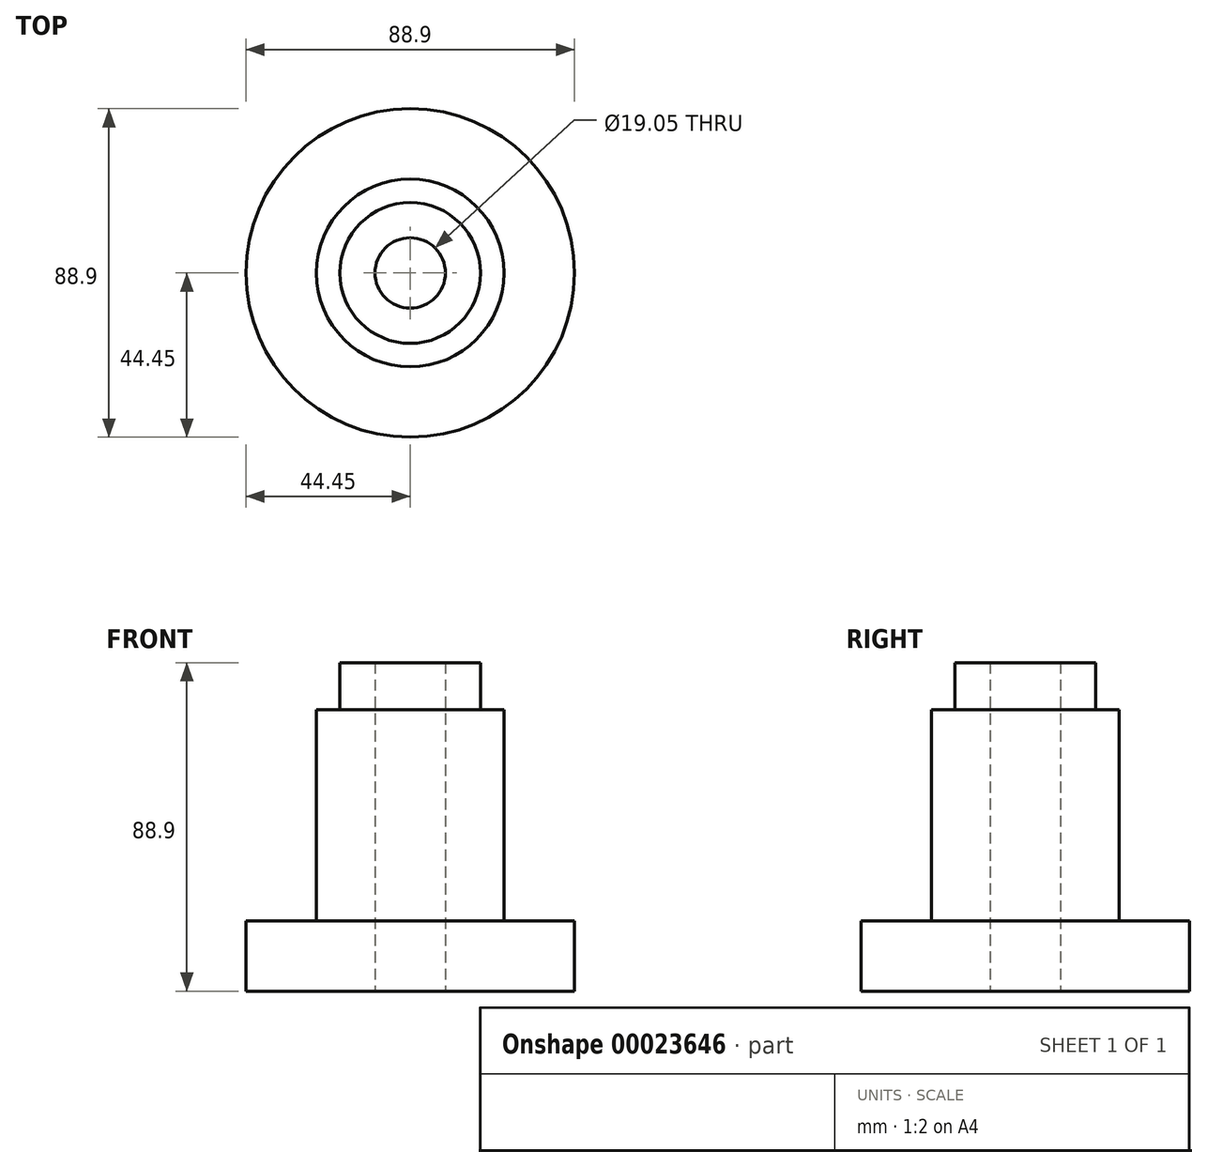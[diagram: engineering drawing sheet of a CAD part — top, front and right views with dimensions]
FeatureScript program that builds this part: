
annotation { "Feature Type Name" : "Feature", "Feature Type Description" : "" }
export const myFeature = defineFeature(function(context is Context, id is Id, definition is map)
    precondition{}
    {
        {
            var Q0;
            Q0=qCreatedBy(makeId("Front.planeOp"),FACE);
            var sketch = newSketch(context, id + "F0", { "sketchPlane" : qUnion([Q0])});
            skLineSegment(sketch, "E0", {"start": v(0, -42.73) * mm, "end": v(0, 46.54) * mm, "construction": true});
            skLineSegment(sketch, "E1.bottom", {"start": v(-9.52, -42.73) * mm, "end": v(-44.45, -42.73) * mm});
            skLineSegment(sketch, "E1.top", {"start": v(-9.52, -23.68) * mm, "end": v(-44.45, -23.68) * mm});
            skLineSegment(sketch, "E1.left", {"start": v(-9.53, -42.73) * mm, "end": v(-9.53, -23.68) * mm});
            skLineSegment(sketch, "E1.right", {"start": v(-44.45, -42.73) * mm, "end": v(-44.45, -23.68) * mm});
            skLineSegment(sketch, "E2.bottom", {"start": v(-9.52, -23.68) * mm, "end": v(-25.4, -23.68) * mm});
            skLineSegment(sketch, "E2.top", {"start": v(-9.53, 33.47) * mm, "end": v(-25.4, 33.47) * mm});
            skLineSegment(sketch, "E2.left", {"start": v(-9.52, -23.68) * mm, "end": v(-9.52, 33.47) * mm});
            skLineSegment(sketch, "E2.right", {"start": v(-25.4, -23.68) * mm, "end": v(-25.4, 33.47) * mm});
            skLineSegment(sketch, "E3.bottom", {"start": v(-9.53, 33.47) * mm, "end": v(-19.05, 33.47) * mm});
            skLineSegment(sketch, "E3.top", {"start": v(-9.53, 46.17) * mm, "end": v(-19.05, 46.17) * mm});
            skLineSegment(sketch, "E3.left", {"start": v(-9.53, 33.47) * mm, "end": v(-9.53, 46.17) * mm});
            skLineSegment(sketch, "E3.right", {"start": v(-19.05, 33.47) * mm, "end": v(-19.05, 46.17) * mm});
            skSolve(sketch);
        }
        {
            var Q0;
            Q0 = qSketchRegion(id + "F0", true);
            var Q1;
            Q1=sQuery(id+"F0.wireOp",EDGE,"E0");
            revolve(context, id + "F1", {"entities" : qUnion([Q0]), "axis" : qUnion([Q1]), "revolveType" : RevolveType.FULL});
        }
    });
